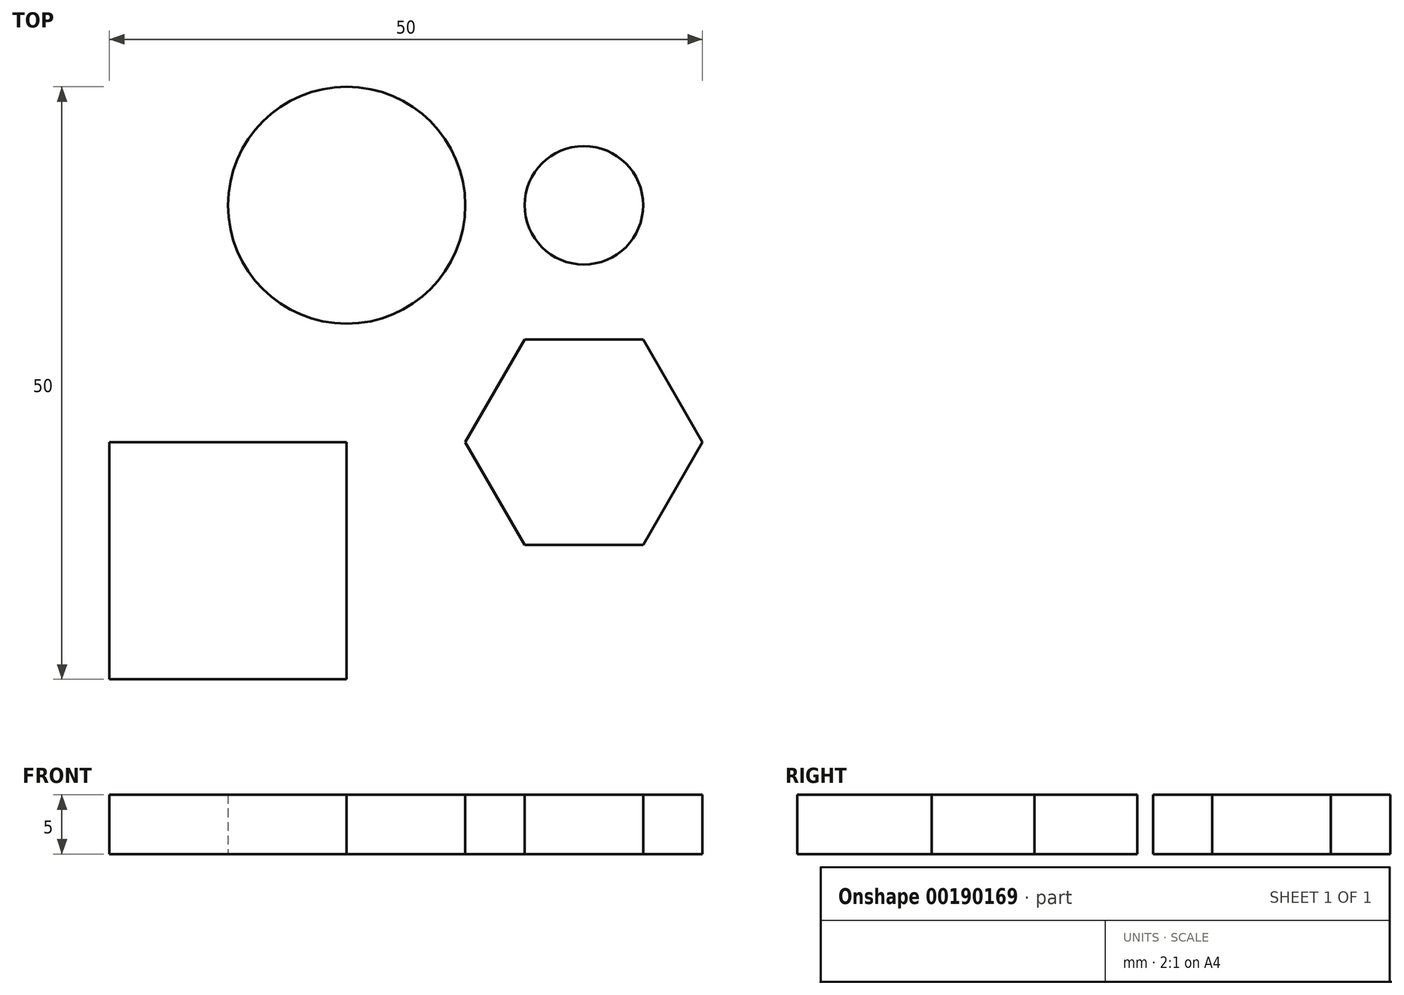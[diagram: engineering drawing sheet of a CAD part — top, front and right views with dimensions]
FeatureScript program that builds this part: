
annotation { "Feature Type Name" : "Feature", "Feature Type Description" : "" }
export const myFeature = defineFeature(function(context is Context, id is Id, definition is map)
    precondition{}
    {
        {
            var Q0;
            Q0=qCreatedBy(makeId("Top.planeOp"),FACE);
            var sketch = newSketch(context, id + "F0", { "sketchPlane" : qUnion([Q0])});
            skLineSegment(sketch, "E0.bottom", {"start": v(0, 0) * mm, "end": v(20, 0) * mm});
            skLineSegment(sketch, "E0.top", {"start": v(0, 20) * mm, "end": v(20, 20) * mm});
            skLineSegment(sketch, "E0.left", {"start": v(0, 0) * mm, "end": v(0, 20) * mm});
            skLineSegment(sketch, "E0.right", {"start": v(20, 0) * mm, "end": v(20, 20) * mm});
            skLineSegment(sketch, "E1.bottom", {"start": v(20, 20) * mm, "end": v(40, 20) * mm, "construction": true});
            skLineSegment(sketch, "E1.top", {"start": v(20, 40) * mm, "end": v(40, 40) * mm, "construction": true});
            skLineSegment(sketch, "E1.left", {"start": v(20, 20) * mm, "end": v(20, 40) * mm, "construction": true});
            skLineSegment(sketch, "E1.right", {"start": v(40, 20) * mm, "end": v(40, 40) * mm, "construction": true});
            skCircle(sketch, "E2", {"center": v(40, 40) * mm, "radius": 5 * mm});
            skCircle(sketch, "E3", {"center": v(20, 40) * mm, "radius": 10 * mm});
            skCircle(sketch, "E4.cCircle", {"center": v(40, 20) * mm, "radius": 8.66 * mm, "construction": true});
            skLineSegment(sketch, "E4.0", {"start": v(45, 11.34) * mm, "end": v(35, 11.34) * mm});
            skLineSegment(sketch, "E4.1", {"start": v(35, 11.34) * mm, "end": v(30, 20) * mm});
            skLineSegment(sketch, "E4.2", {"start": v(30, 20) * mm, "end": v(35, 28.66) * mm});
            skLineSegment(sketch, "E4.3", {"start": v(35, 28.66) * mm, "end": v(45, 28.66) * mm});
            skLineSegment(sketch, "E4.4", {"start": v(45, 28.66) * mm, "end": v(50, 20) * mm});
            skLineSegment(sketch, "E4.5", {"start": v(50, 20) * mm, "end": v(45, 11.34) * mm});
            skPoint(sketch, "E4.0.midPoint", {"position": v(40, 11.34) * mm});
            skCircle(sketch, "E5", {"center": v(40, 0) * mm, "radius": 3 * mm});
            skCircle(sketch, "E6.1.0.0", {"center": v(50, 0) * mm, "radius": 3 * mm});
            skCircle(sketch, "E6.2.0.0", {"center": v(60, 0) * mm, "radius": 3 * mm});
            skCircle(sketch, "E6.3.0.0", {"center": v(70, 0) * mm, "radius": 3 * mm});
            skCircle(sketch, "E6.4.0.0", {"center": v(80, 0) * mm, "radius": 3 * mm});
            skCircle(sketch, "E6.5.0.0", {"center": v(90, 0) * mm, "radius": 3 * mm});
            skCircle(sketch, "E6.6.0.0", {"center": v(100, 0) * mm, "radius": 3 * mm});
            skCircle(sketch, "E6.7.0.0", {"center": v(110, 0) * mm, "radius": 3 * mm});
            skCircle(sketch, "E6.8.0.0", {"center": v(120, 0) * mm, "radius": 3 * mm});
            skCircle(sketch, "E6.9.0.0", {"center": v(130, 0) * mm, "radius": 3 * mm});
            skCircle(sketch, "E6.10.0.0", {"center": v(140, 0) * mm, "radius": 3 * mm});
            skCircle(sketch, "E6.11.0.0", {"center": v(150, 0) * mm, "radius": 3 * mm});
            skCircle(sketch, "E6.12.0.0", {"center": v(160, 0) * mm, "radius": 3 * mm});
            skCircle(sketch, "E6.13.0.0", {"center": v(170, 0) * mm, "radius": 3 * mm});
            skCircle(sketch, "E6.14.0.0", {"center": v(180, 0) * mm, "radius": 3 * mm});
            skCircle(sketch, "E6.15.0.0", {"center": v(190, 0) * mm, "radius": 3 * mm});
            skCircle(sketch, "E6.16.0.0", {"center": v(200, 0) * mm, "radius": 3 * mm});
            skCircle(sketch, "E6.17.0.0", {"center": v(210, 0) * mm, "radius": 3 * mm});
            skCircle(sketch, "E6.18.0.0", {"center": v(220, 0) * mm, "radius": 3 * mm});
            skCircle(sketch, "E6.19.0.0", {"center": v(230, 0) * mm, "radius": 3 * mm});
            skCircle(sketch, "E6.20.0.0", {"center": v(240, 0) * mm, "radius": 3 * mm});
            skCircle(sketch, "E6.21.0.0", {"center": v(250, 0) * mm, "radius": 3 * mm});
            skCircle(sketch, "E6.22.0.0", {"center": v(260, 0) * mm, "radius": 3 * mm});
            skCircle(sketch, "E6.23.0.0", {"center": v(270, 0) * mm, "radius": 3 * mm});
            skCircle(sketch, "E6.24.0.0", {"center": v(280, 0) * mm, "radius": 3 * mm});
            skLineSegment(sketch, "E6.direction1", {"start": v(40, 0) * mm, "end": v(50, 0) * mm, "construction": true});
            skCircle(sketch, "E7", {"center": v(30, 0) * mm, "radius": 3 * mm});
            skSolve(sketch);
        }
        {
            var Q0;
            Q0=makeQuery(id+"F0.imprint","IMPRINT",FACE,{"disambiguationData":[TD([[makeQuery(id+"F0.imprint","IMPRINT",EDGE,{"derivedFrom":sQuery(id+"F0.wireOp",EDGE,"E0.bottom")}),1.0]])]});
            var Q1;
            Q1=makeQuery(id+"F0.imprint","IMPRINT",FACE,{"disambiguationData":[TD([[makeQuery(id+"F0.imprint","IMPRINT",EDGE,{"derivedFrom":sQuery(id+"F0.wireOp",EDGE,"E4.0")}),-1.0]])]});
            var Q2;
            Q2=makeQuery(id+"F0.imprint","IMPRINT",FACE,{"disambiguationData":[TD([[makeQuery(id+"F0.imprint","IMPRINT",EDGE,{"derivedFrom":sQuery(id+"F0.wireOp",EDGE,"E2")}),1.0]])]});
            var Q3;
            Q3=makeQuery(id+"F0.imprint","IMPRINT",FACE,{"disambiguationData":[TD([[makeQuery(id+"F0.imprint","IMPRINT",EDGE,{"derivedFrom":sQuery(id+"F0.wireOp",EDGE,"E3")}),1.0]])]});
            extrude(context, id + "F1", {"entities" : qUnion([Q0, Q1, Q2, Q3]), "depth" : 5 * mm});
        }
    });
